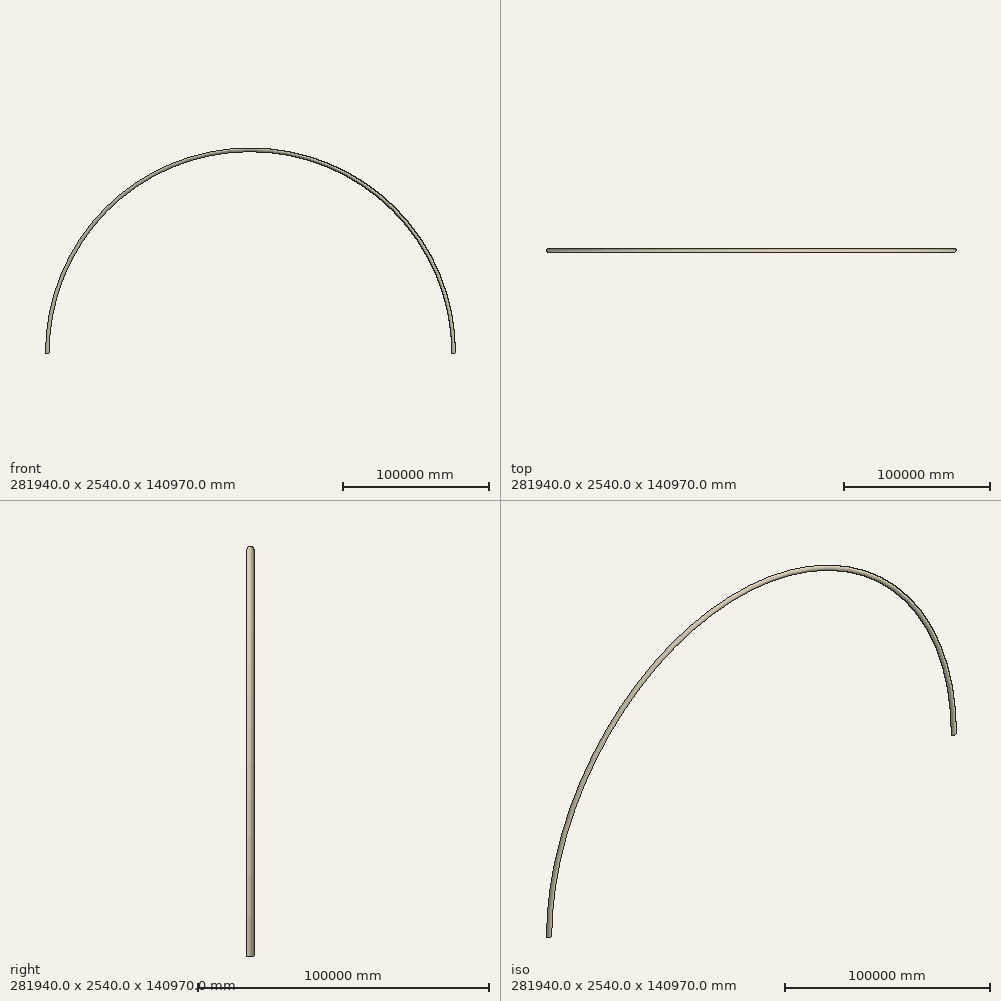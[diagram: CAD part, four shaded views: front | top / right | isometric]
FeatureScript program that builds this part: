
annotation { "Feature Type Name" : "Feature", "Feature Type Description" : "" }
export const myFeature = defineFeature(function(context is Context, id is Id, definition is map)
    precondition{}
    {
        {
            var Q0;
            Q0=qCreatedBy(makeId("Right.planeOp"),FACE);
            var sketch = newSketch(context, id + "F0", { "sketchPlane" : qUnion([Q0])});
            skCircle(sketch, "E0", {"center": v(0, 139700) * mm, "radius": 1270 * mm});
            skCircle(sketch, "E1", {"center": v(0, 139700) * mm, "radius": 1016 * mm});
            skLineSegment(sketch, "E2", {"start": v(0, 0) * mm, "end": v(126270.53, 0) * mm, "construction": true});
            skSolve(sketch);
        }
        {
            var Q0;
            Q0 = qSketchRegion(id + "F0", true);
            var Q1;
            Q1=sQuery(id+"F0.wireOp",EDGE,"E2");
            revolve(context, id + "F1", {"surfaceOperationType" : NewSurfaceOperationType.NEW, "entities" : qUnion([Q0]), "axis" : qUnion([Q1]), "revolveType" : RevolveType.TWO_DIRECTIONS, "angle" : 90 * degree, "angleBack" : 270 * degree});
        }
    });
